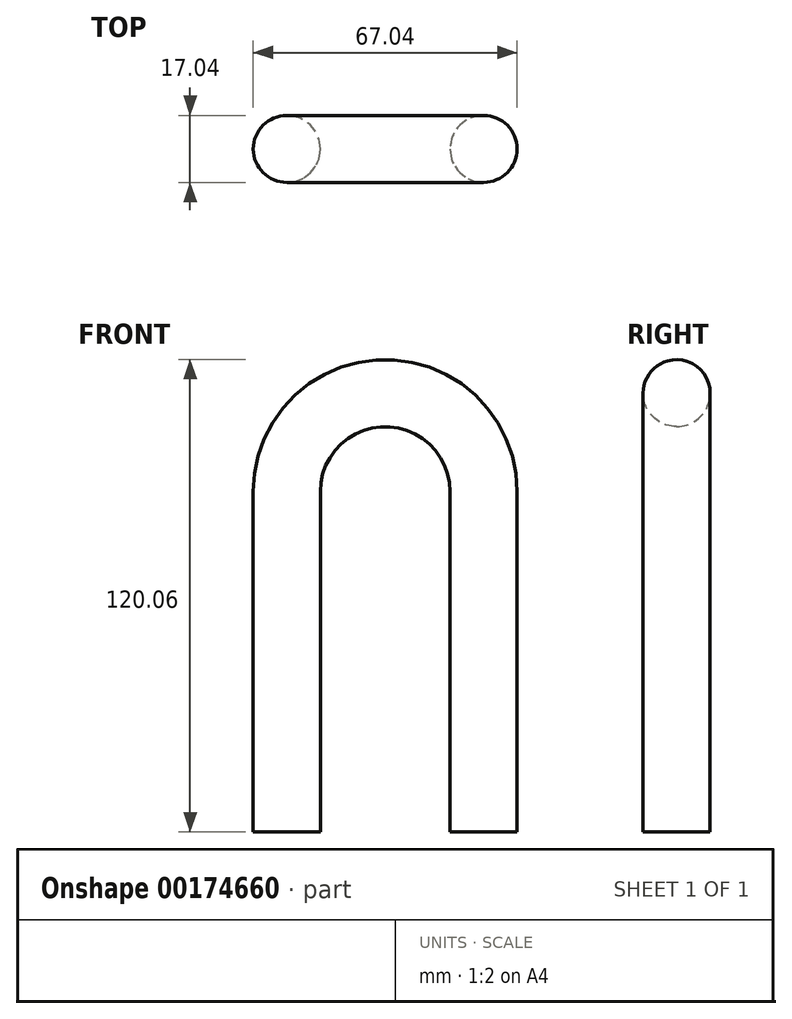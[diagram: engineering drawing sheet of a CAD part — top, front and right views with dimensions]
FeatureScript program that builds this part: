
annotation { "Feature Type Name" : "Feature", "Feature Type Description" : "" }
export const myFeature = defineFeature(function(context is Context, id is Id, definition is map)
    precondition{}
    {
        {
            var Q0;
            Q0=qCreatedBy(makeId("Front.planeOp"),FACE);
            var sketch = newSketch(context, id + "F0", { "sketchPlane" : qUnion([Q0])});
            skLineSegment(sketch, "E0.left", {"start": v(25, -43.27) * mm, "end": v(25, 43.27) * mm});
            skLineSegment(sketch, "E0.right", {"start": v(-25, -43.27) * mm, "end": v(-25, 43.27) * mm});
            skPoint(sketch, "E0.middle", {"position": v(0, 0) * mm});
            skPoint(sketch, "E1.center.orphan", {"position": v(0, 43.27) * mm});
            skArc(sketch, "E2", {"start": v(25, 43.27) * mm, "mid": v(0, 68.27) * mm, "end": v(-25, 43.27) * mm});
            skSolve(sketch);
        }
        {
            var Q0;
            Q0=qCreatedBy(makeId("Top.planeOp"),FACE);
            var Q1;
            Q1=sQuery(id+"F0.wireOp",VERTEX,"E0.left.start");
            cPlane(context, id + "F1", {"entities" : qUnion([Q0, Q1]), "cplaneType" : CPlaneType.PLANE_POINT, "offset" : 25 * mm, "width" : 150 * mm, "height" : 150 * mm});
        }
        {
            var Q0;
            Q0=qCreatedBy(id+"F1.planeOp",FACE);
            var sketch = newSketch(context, id + "F2", { "sketchPlane" : qUnion([Q0])});
            skCircle(sketch, "E3", {"center": v(-25, 0) * mm, "radius": 8.52 * mm});
            skSolve(sketch);
        }
        {
            var Q0;
            Q0=makeQuery(id+"F2.imprint","IMPRINT",FACE,{"disambiguationData":[TD([[makeQuery(id+"F2.imprint","IMPRINT",EDGE,{"derivedFrom":sQuery(id+"F2.wireOp",EDGE,"E3")}),1.0]])]});
            var Q1;
            Q1=sQuery(id+"F0.wireOp",EDGE,"E0.right");
            var Q2;
            Q2=sQuery(id+"F0.wireOp",EDGE,"E2");
            var Q3;
            Q3=sQuery(id+"F0.wireOp",EDGE,"E0.left");
            sweep(context, id + "F3", {"profiles" : qUnion([Q0]), "path" : qUnion([Q1, Q2, Q3])});
        }
    });
